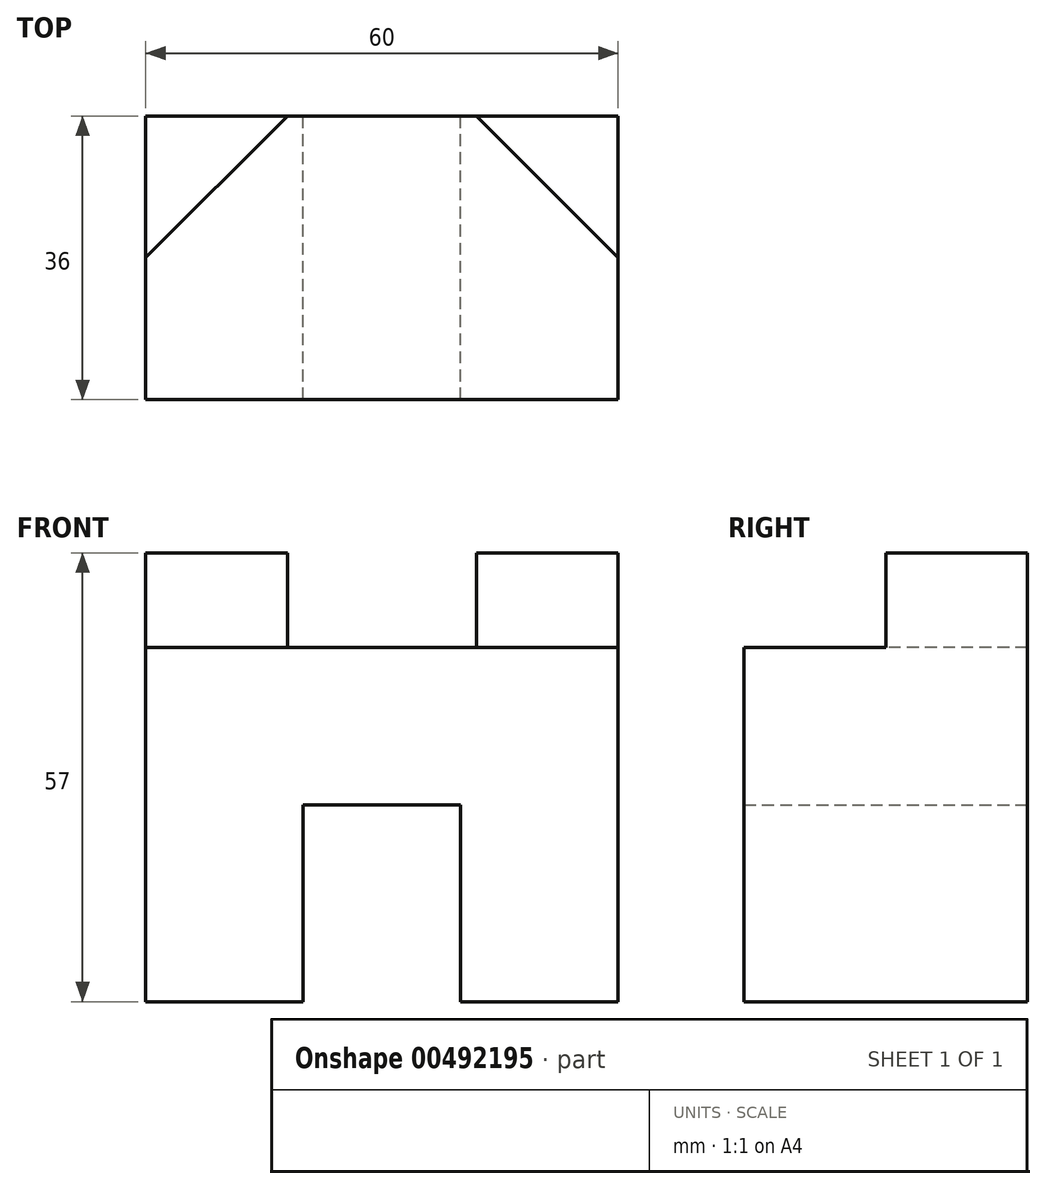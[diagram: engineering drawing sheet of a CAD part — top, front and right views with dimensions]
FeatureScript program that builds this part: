
annotation { "Feature Type Name" : "Feature", "Feature Type Description" : "" }
export const myFeature = defineFeature(function(context is Context, id is Id, definition is map)
    precondition{}
    {
        {
            var Q0;
            Q0=qCreatedBy(makeId("Front.planeOp"),FACE);
            var sketch = newSketch(context, id + "F0", { "sketchPlane" : qUnion([Q0])});
            skLineSegment(sketch, "E0.bottom", {"start": v(-30, -22.5) * mm, "end": v(-10, -22.5) * mm});
            skLineSegment(sketch, "E0.top", {"start": v(-30, 22.5) * mm, "end": v(30, 22.5) * mm});
            skLineSegment(sketch, "E0.left", {"start": v(-30, -22.5) * mm, "end": v(-30, 22.5) * mm});
            skLineSegment(sketch, "E0.right", {"start": v(30, -22.5) * mm, "end": v(30, 22.5) * mm});
            skPoint(sketch, "E0.middle", {"position": v(0, 0) * mm});
            skLineSegment(sketch, "E1.top", {"start": v(-10, 2.5) * mm, "end": v(10, 2.5) * mm});
            skLineSegment(sketch, "E1.left", {"start": v(-10, -22.5) * mm, "end": v(-10, 2.5) * mm});
            skLineSegment(sketch, "E1.right", {"start": v(10, -22.5) * mm, "end": v(10, 2.5) * mm});
            skPoint(sketch, "E1.middle", {"position": v(0, -22.5) * mm});
            skLineSegment(sketch, "E2.trimOffspring", {"start": v(10, -22.5) * mm, "end": v(30, -22.5) * mm});
            skPoint(sketch, "E1.bottom.end.orphan", {"position": v(10, -47.5) * mm});
            skPoint(sketch, "E3.orphan", {"position": v(-10, -47.5) * mm});
            skLineSegment(sketch, "E4.bottom", {"start": v(-10, 22.5) * mm, "end": v(-30, 22.5) * mm});
            skPoint(sketch, "E5.oppositeSnap0", {"position": v(-20, 34.5) * mm});
            skLineSegment(sketch, "E5.bottom", {"start": v(10, 22.5) * mm, "end": v(30, 22.5) * mm});
            skSolve(sketch);
        }
        {
            var Q0;
            Q0 = qSketchRegion(id + "F0", true);
            extrude(context, id + "F1", {"entities" : qUnion([Q0]), "depth" : 36 * mm});
        }
        {
            var Q0;
            Q0=makeQuery(id+"F1.opExtrude","SWEPT_FACE",FACE,{"disambiguationData":[OSD([sQuery(id+"F0.wireOp",EDGE,"E0.top"),sQuery(id+"F0.wireOp",EDGE,"E4.bottom"),sQuery(id+"F0.wireOp",EDGE,"E5.bottom")])]});
            var sketch = newSketch(context, id + "F2", { "sketchPlane" : qUnion([Q0])});
            skLineSegment(sketch, "E6.left", {"start": v(-12, 0) * mm, "end": v(-12, 0) * mm});
            skLineSegment(sketch, "E6.right", {"start": v(12, 0) * mm, "end": v(12, 0) * mm});
            skPoint(sketch, "E6.middle", {"position": v(0, 0) * mm});
            skLineSegment(sketch, "E7", {"start": v(-12, 0) * mm, "end": v(-30, -18) * mm});
            skLineSegment(sketch, "E8", {"start": v(12, 0) * mm, "end": v(30, -18) * mm});
            skSolve(sketch);
        }
        {
            var Q0;
            {var subQ0=sQuery(id+"F2.wireOp",EDGE,"E7");Q0=makeQuery(id+"F2.imprint","IMPRINT",FACE,{"disambiguationData":[TD([[makeQuery(id+"F2.imprint","IMPRINT",EDGE,{"derivedFrom":subQ0}),-1.0]])]});}
            var Q1;
            {var subQ0=sQuery(id+"F2.wireOp",EDGE,"E8");Q1=makeQuery(id+"F2.imprint","IMPRINT",FACE,{"disambiguationData":[TD([[makeQuery(id+"F2.imprint","IMPRINT",EDGE,{"derivedFrom":subQ0}),1.0]])]});}
            extrude(context, id + "F3", {"entities" : qUnion([Q0, Q1]), "operationType" : NewBodyOperationType.ADD, "depth" : 12 * mm});
        }
    });
